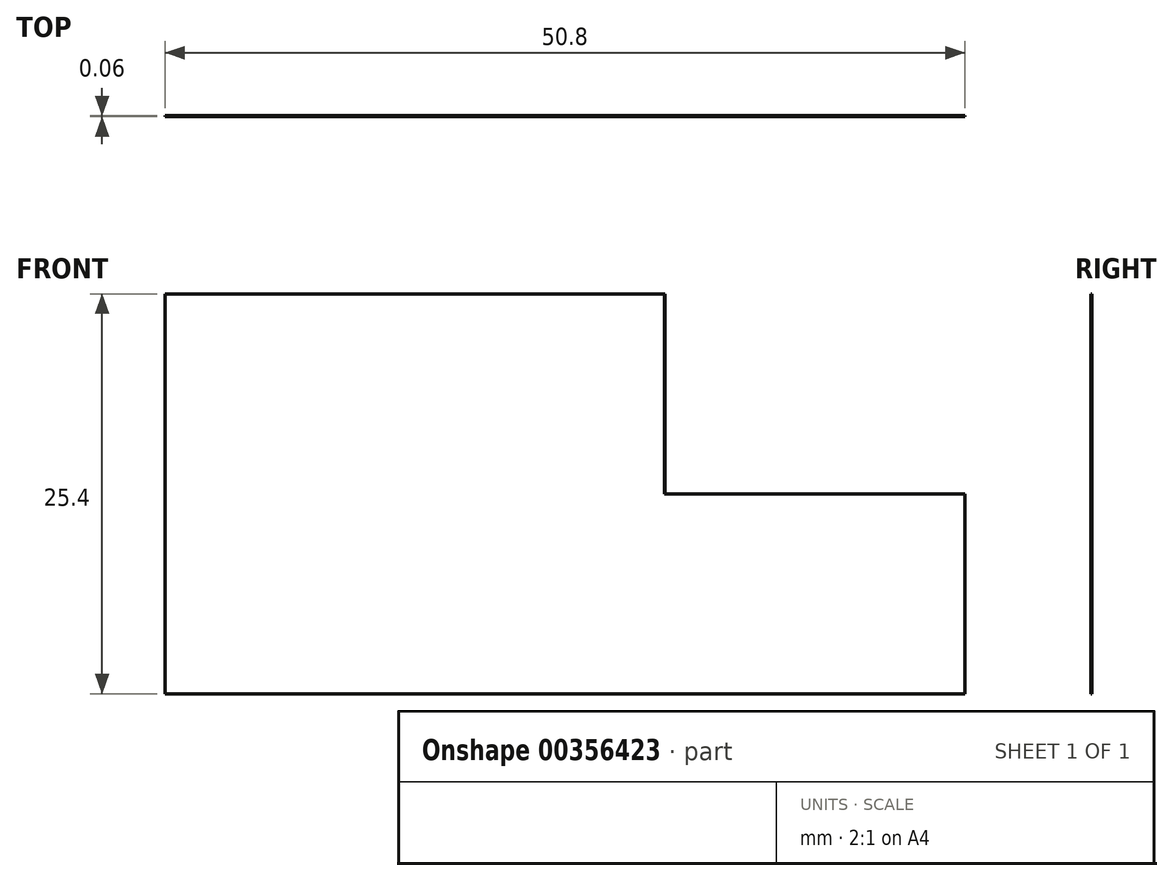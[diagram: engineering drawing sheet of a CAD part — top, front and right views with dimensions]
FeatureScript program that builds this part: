
annotation { "Feature Type Name" : "Feature", "Feature Type Description" : "" }
export const myFeature = defineFeature(function(context is Context, id is Id, definition is map)
    precondition{}
    {
        {
            var Q0;
            Q0=qCreatedBy(makeId("Front.planeOp"),FACE);
            var sketch = newSketch(context, id + "F0", { "sketchPlane" : qUnion([Q0])});
            skLineSegment(sketch, "E0", {"start": v(0, 25.4) * mm, "end": v(0, 0) * mm});
            skLineSegment(sketch, "E1", {"start": v(0, 0) * mm, "end": v(50.8, 0) * mm});
            skLineSegment(sketch, "E2", {"start": v(50.8, 0) * mm, "end": v(50.8, 25.4) * mm});
            skLineSegment(sketch, "E3", {"start": v(50.8, 25.4) * mm, "end": v(0, 25.4) * mm});
            skSolve(sketch);
        }
        {
            var Q0;
            Q0 = qSketchRegion(id + "F0", true);
            extrude(context, id + "F1", {"entities" : qUnion([Q0]), "depth" : 6 / 101.6 * mm});
        }
        {
            var Q0;
            Q0=makeQuery(id+"F1.opExtrude","SWEPT_FACE",FACE,{"disambiguationData":[OSD([sQuery(id+"F0.wireOp",EDGE,"E3")])]});
            var sketch = newSketch(context, id + "F2", { "sketchPlane" : qUnion([Q0])});
            skLineSegment(sketch, "E4", {"start": v(6.35, -38.1) * mm, "end": v(31.75, 0) * mm});
            skLineSegment(sketch, "E5", {"start": v(44.45, -38.1) * mm, "end": v(50.8, -19.05) * mm});
            skSolve(sketch);
        }
        {
            var Q0;
            Q0 = qSketchRegion(id + "F2", true);
            var Q1;
            {var subQ5=sQuery(id+"F2.wireOp",EDGE,"E4");Q1=makeQuery(id+"F2.imprint","IMPRINT",FACE,{"disambiguationData":[TD([[makeQuery(id+"F2.imprint","IMPRINT",EDGE,{"derivedFrom":subQ5}),-1.0]])]});}
            extrude(context, id + "F3", {"entities" : qUnion([Q0, Q1]), "operationType" : NewBodyOperationType.REMOVE, "oppositeDirection" : true, "depth" : 12.7 * mm});
        }
    });
